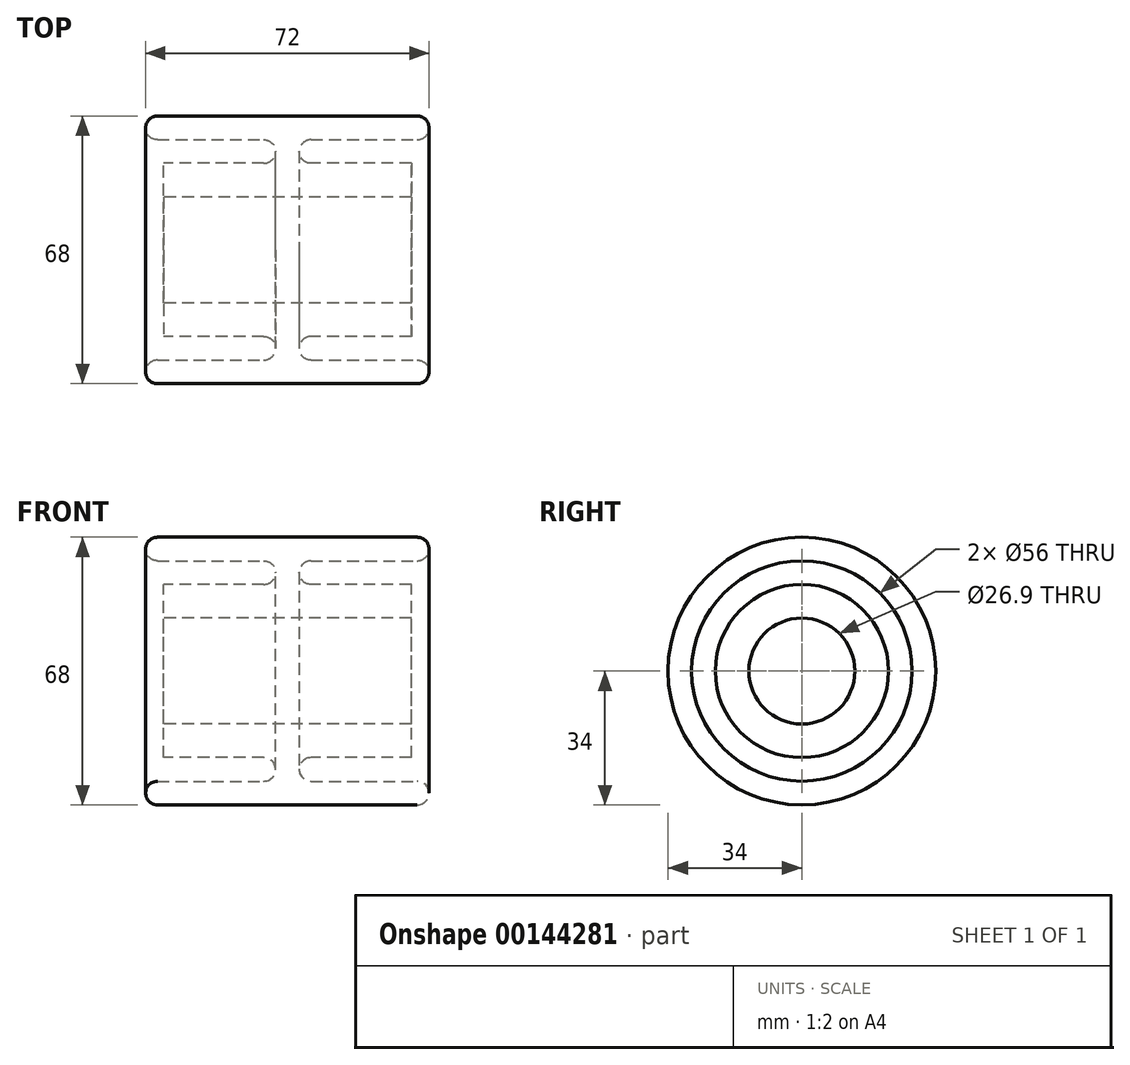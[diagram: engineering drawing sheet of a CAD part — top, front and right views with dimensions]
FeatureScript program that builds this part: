
annotation { "Feature Type Name" : "Feature", "Feature Type Description" : "" }
export const myFeature = defineFeature(function(context is Context, id is Id, definition is map)
    precondition{}
    {
        {
            var Q0;
            Q0=qCreatedBy(makeId("Right.planeOp"),FACE);
            var sketch = newSketch(context, id + "F0", { "sketchPlane" : qUnion([Q0])});
            skCircle(sketch, "E0", {"center": v(0, 0) * mm, "radius": 13.45 * mm});
            skCircle(sketch, "E1", {"center": v(0, 0) * mm, "radius": 22 * mm});
            skSolve(sketch);
        }
        {
            var Q0;
            Q0 = qSketchRegion(id + "F0", true);
            extrude(context, id + "F1", {"entities" : qUnion([Q0]), "depth" : 63 * mm});
        }
        {
            var Q0;
            Q0=qCreatedBy(makeId("Front.planeOp"),FACE);
            var sketch = newSketch(context, id + "F2", { "sketchPlane" : qUnion([Q0])});
            skLineSegment(sketch, "E2", {"start": v(31.5, 0) * mm, "end": v(31.5, 25.59) * mm, "construction": true});
            skLineSegment(sketch, "E3", {"start": v(-1.5, 34) * mm, "end": v(64.5, 34) * mm});
            skArc(sketch, "E4", {"start": v(-1.5, 34) * mm, "mid": v(-4.5, 31) * mm, "end": v(-1.5, 28) * mm});
            skArc(sketch, "E5", {"start": v(64.5, 34) * mm, "mid": v(67.5, 31) * mm, "end": v(64.5, 28) * mm});
            skLineSegment(sketch, "E6", {"start": v(-1.5, 28) * mm, "end": v(25.5, 28) * mm});
            skLineSegment(sketch, "E7", {"start": v(64.5, 28) * mm, "end": v(37.5, 28) * mm});
            skLineSegment(sketch, "E8", {"start": v(0, 22) * mm, "end": v(63, 22) * mm, "construction": true});
            skArc(sketch, "E9", {"start": v(25.5, 28) * mm, "mid": v(28.5, 25) * mm, "end": v(25.5, 22) * mm});
            skArc(sketch, "E10", {"start": v(37.5, 28) * mm, "mid": v(34.5, 25) * mm, "end": v(37.5, 22) * mm});
            skLineSegment(sketch, "E11", {"start": v(25.5, 22) * mm, "end": v(37.5, 22) * mm});
            skSolve(sketch);
        }
        {
            var Q0;
            Q0 = qSketchRegion(id + "F2", true);
            var Q1;
            Q1=makeQuery(id+"F1.opExtrude","SWEPT_FACE",FACE,{"disambiguationData":[OSD([sQuery(id+"F0.wireOp",EDGE,"E1")])]});
            revolve(context, id + "F3", {"operationType" : NewBodyOperationType.ADD, "entities" : qUnion([Q0]), "axis" : qUnion([Q1]), "revolveType" : RevolveType.FULL});
        }
    });
